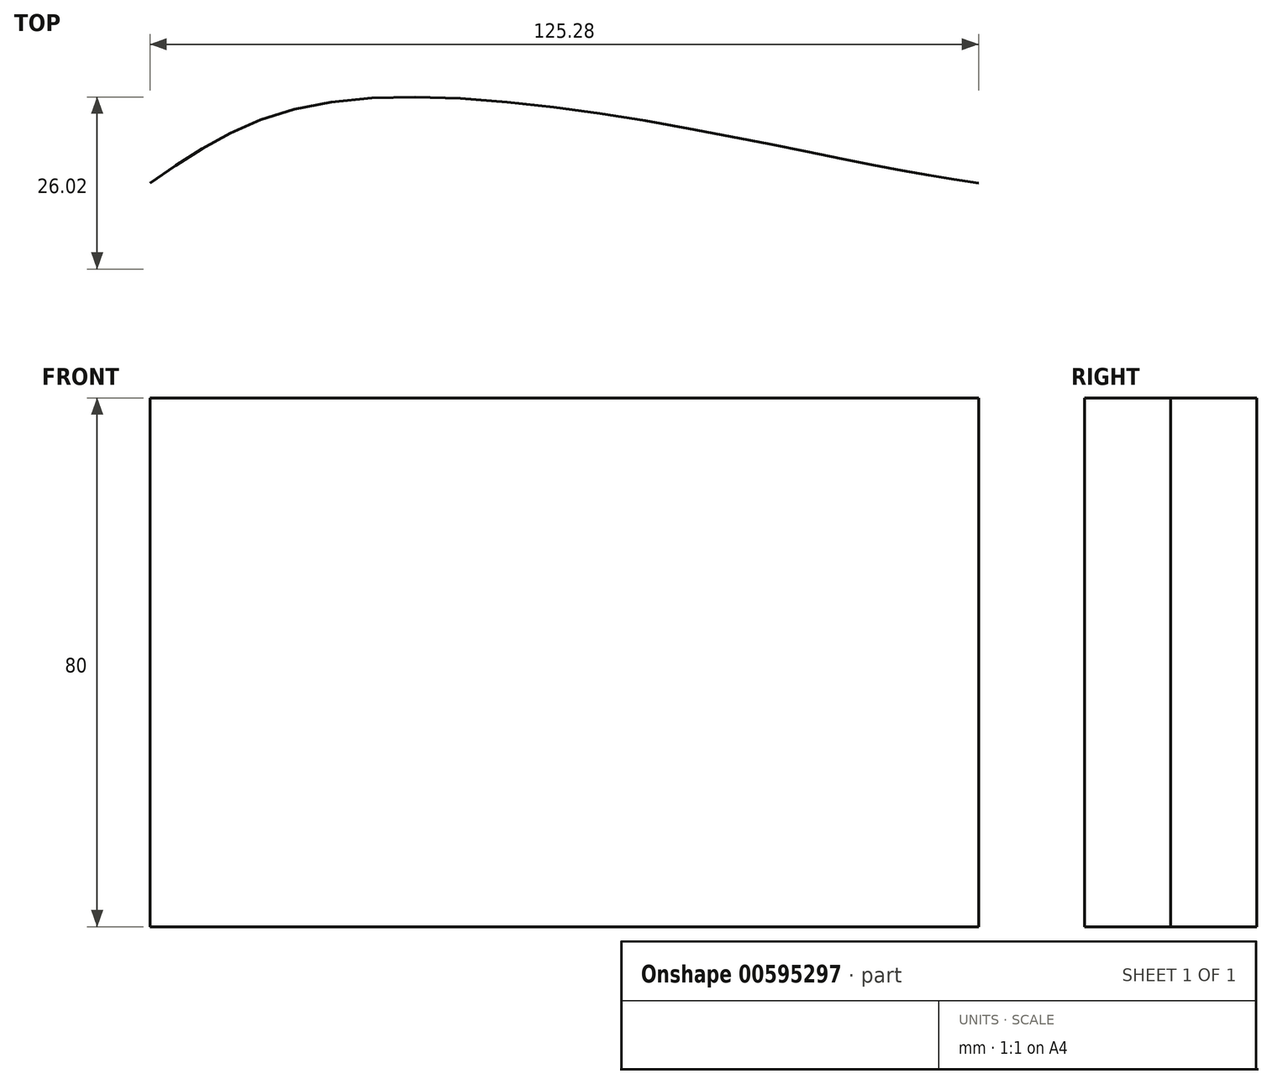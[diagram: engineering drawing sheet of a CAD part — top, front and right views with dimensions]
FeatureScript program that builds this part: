
annotation { "Feature Type Name" : "Feature", "Feature Type Description" : "" }
export const myFeature = defineFeature(function(context is Context, id is Id, definition is map)
    precondition{}
    {
        {
            var Q0;
            Q0=qCreatedBy(makeId("Top.planeOp"),FACE);
            var sketch = newSketch(context, id + "F0", { "sketchPlane" : qUnion([Q0])});
            skFitSpline(sketch, "E0", {"points": [v(-62.49, 0) * mm, v(-39.6, 11.44) * mm, v(7.38, 10.24) * mm, v(45.32, 3.01) * mm, v(62.79, 0) * mm], "startDerivative": vector(88.81, 61.49) * mm, "endDerivative": vector(84.9, -13.43) * mm});
            skLineSegment(sketch, "E1", {"start": v(-68.51, 0) * mm, "end": v(71.82, 0) * mm});
            skFitSpline(sketch, "E2.MirrorCS", {"points": [v(-62.49, 0) * mm, v(-39.6, -11.44) * mm, v(7.38, -10.24) * mm, v(45.32, -3.01) * mm, v(62.79, 0) * mm], "startDerivative": vector(88.81, -61.49) * mm, "endDerivative": vector(84.9, 13.43) * mm});
            skSolve(sketch);
        }
        {
            var Q0;
            {var subQ0=sQuery(id+"F0.wireOp",EDGE,"E0");Q0=makeQuery(id+"F0.imprint","IMPRINT",FACE,{"disambiguationData":[TD([[makeQuery(id+"F0.imprint","IMPRINT",EDGE,{"derivedFrom":subQ0}),-1.0]])]});}
            var Q1;
            {var subQ0=sQuery(id+"F0.wireOp",EDGE,"E2.MirrorCS");Q1=makeQuery(id+"F0.imprint","IMPRINT",FACE,{"disambiguationData":[TD([[makeQuery(id+"F0.imprint","IMPRINT",EDGE,{"derivedFrom":subQ0}),1.0]])]});}
            extrude(context, id + "F1", {"entities" : qUnion([Q0, Q1]), "depth" : 80 * mm, "offsetDistance" : 25 * mm});
        }
    });
